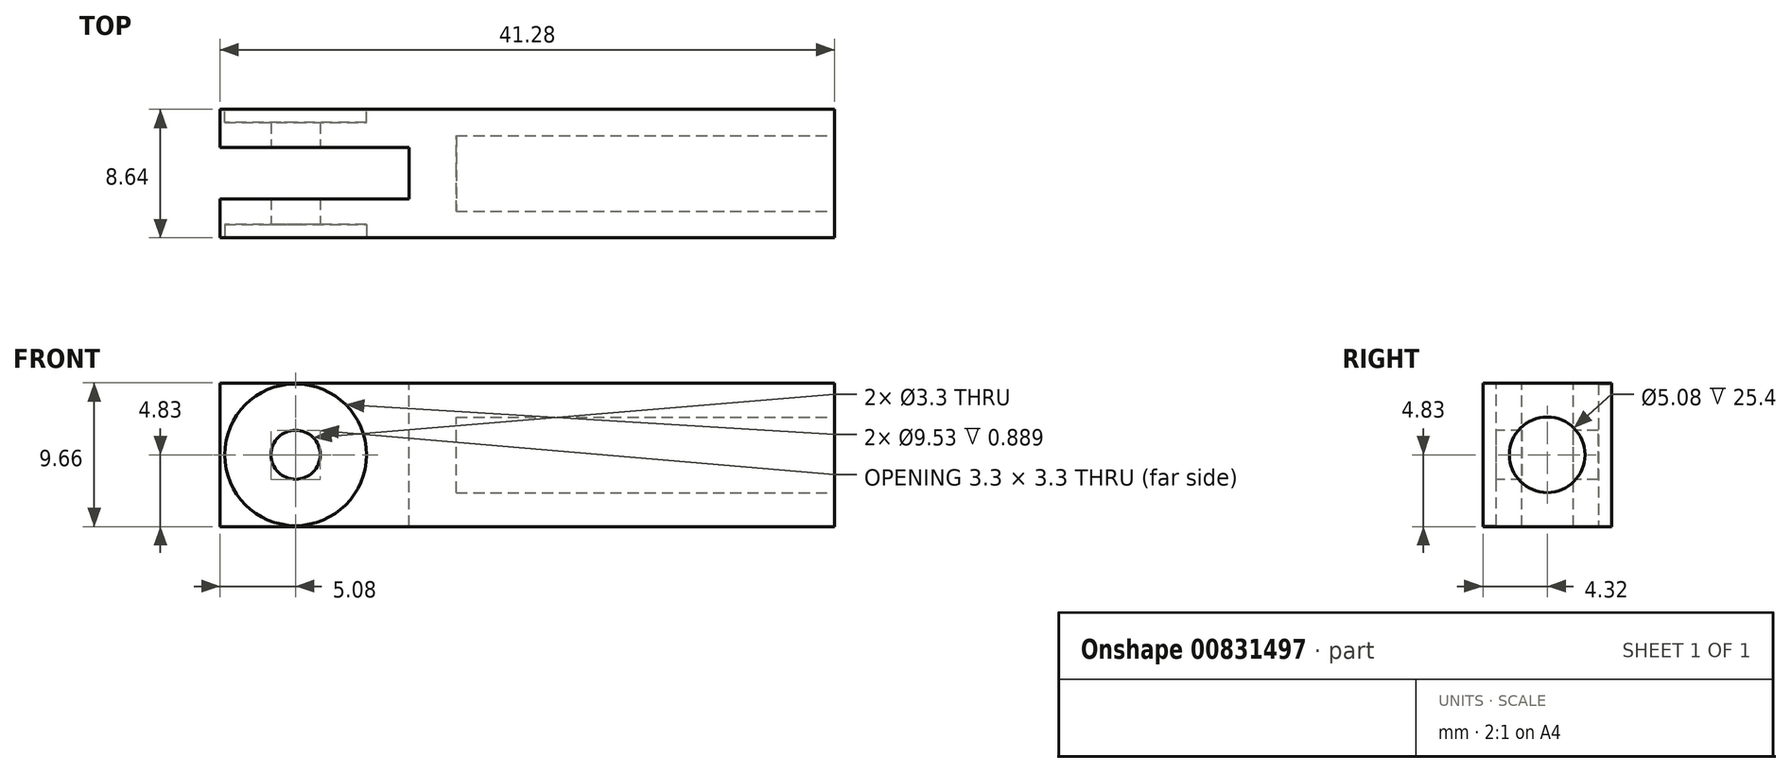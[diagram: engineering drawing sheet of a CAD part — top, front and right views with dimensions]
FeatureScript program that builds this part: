
annotation { "Feature Type Name" : "Feature", "Feature Type Description" : "" }
export const myFeature = defineFeature(function(context is Context, id is Id, definition is map)
    precondition{}
    {
        {
            var Q0;
            Q0=qCreatedBy(makeId("Right.planeOp"),FACE);
            var sketch = newSketch(context, id + "F0", { "sketchPlane" : qUnion([Q0])});
            skLineSegment(sketch, "E0.bottom", {"start": v(4.32, -4.83) * mm, "end": v(-4.32, -4.83) * mm});
            skLineSegment(sketch, "E0.top", {"start": v(4.32, 4.83) * mm, "end": v(-4.32, 4.83) * mm});
            skLineSegment(sketch, "E0.left", {"start": v(4.32, -4.83) * mm, "end": v(4.32, 4.83) * mm});
            skLineSegment(sketch, "E0.right", {"start": v(-4.32, -4.83) * mm, "end": v(-4.32, 4.83) * mm});
            skPoint(sketch, "E0.middle", {"position": v(0, 0) * mm});
            skSolve(sketch);
        }
        {
            var Q0;
            Q0 = qSketchRegion(id + "F0", true);
            extrude(context, id + "F1", {"entities" : qUnion([Q0]), "depth" : 41.27 * mm, "offsetDistance" : 25.4 * mm});
        }
        {
            var Q0;
            Q0=makeQuery(id+"F1.opExtrude","CAP_FACE",FACE,{"disambiguationData":[OSD([sQuery(id+"F0.wireOp",EDGE,"E0.bottom"),sQuery(id+"F0.wireOp",EDGE,"E0.top"),sQuery(id+"F0.wireOp",EDGE,"E0.left"),sQuery(id+"F0.wireOp",EDGE,"E0.right")])],"isStart":false});
            var sketch = newSketch(context, id + "F2", { "sketchPlane" : qUnion([Q0])});
            skCircle(sketch, "E1", {"center": v(0, 0) * mm, "radius": 2.54 * mm});
            skSolve(sketch);
        }
        {
            var Q0;
            Q0 = qSketchRegion(id + "F2", true);
            extrude(context, id + "F3", {"entities" : qUnion([Q0]), "operationType" : NewBodyOperationType.REMOVE, "oppositeDirection" : true, "depth" : 25.4 * mm, "offsetDistance" : 25.4 * mm});
        }
        {
            var Q0;
            Q0=makeQuery(id+"F1.opExtrude","SWEPT_FACE",FACE,{"disambiguationData":[OSD([sQuery(id+"F0.wireOp",EDGE,"E0.top")])]});
            var sketch = newSketch(context, id + "F4", { "sketchPlane" : qUnion([Q0])});
            skPoint(sketch, "E2.middle", {"position": v(0, 0) * mm});
            skLineSegment(sketch, "E3", {"start": v(0, 1.77) * mm, "end": v(12.71, 1.77) * mm});
            skLineSegment(sketch, "E4", {"start": v(12.71, 1.77) * mm, "end": v(12.71, -1.7) * mm});
            skLineSegment(sketch, "E5", {"start": v(12.71, -1.7) * mm, "end": v(0, -1.7) * mm});
            skSolve(sketch);
        }
        {
            var Q0;
            Q0=makeQuery(id+"F1.opExtrude","SWEPT_FACE",FACE,{"disambiguationData":[OSD([sQuery(id+"F0.wireOp",EDGE,"E0.right")])]});
            var sketch = newSketch(context, id + "F5", { "sketchPlane" : qUnion([Q0])});
            skCircle(sketch, "E6", {"center": v(5.08, 0) * mm, "radius": 1.65 * mm});
            skSolve(sketch);
        }
        {
            var Q0;
            Q0 = qSketchRegion(id + "F5", true);
            extrude(context, id + "F6", {"entities" : qUnion([Q0]), "operationType" : NewBodyOperationType.REMOVE, "oppositeDirection" : true, "depth" : 8.64 * mm, "offsetDistance" : 25.4 * mm});
        }
        {
            var Q0;
            Q0=makeQuery(id+"F1.opExtrude","SWEPT_FACE",FACE,{"disambiguationData":[OSD([sQuery(id+"F0.wireOp",EDGE,"E0.right")])]});
            var sketch = newSketch(context, id + "F7", { "sketchPlane" : qUnion([Q0])});
            skCircle(sketch, "E7", {"center": v(5.08, 0) * mm, "radius": 4.76 * mm});
            skSolve(sketch);
        }
        {
            var Q0;
            Q0 = qSketchRegion(id + "F7", true);
            extrude(context, id + "F8", {"entities" : qUnion([Q0]), "operationType" : NewBodyOperationType.REMOVE, "oppositeDirection" : true, "depth" : 0.89 * mm, "offsetDistance" : 25.4 * mm});
        }
        {
            var Q0;
            Q0=makeQuery(id+"F1.opExtrude","SWEPT_FACE",FACE,{"disambiguationData":[OSD([sQuery(id+"F0.wireOp",EDGE,"E0.left")])]});
            var sketch = newSketch(context, id + "F9", { "sketchPlane" : qUnion([Q0])});
            skCircle(sketch, "E8", {"center": v(-5.08, 0) * mm, "radius": 4.76 * mm});
            skSolve(sketch);
        }
        {
            var Q0;
            Q0 = qSketchRegion(id + "F9", true);
            extrude(context, id + "F10", {"entities" : qUnion([Q0]), "operationType" : NewBodyOperationType.REMOVE, "oppositeDirection" : true, "depth" : 0.89 * mm, "offsetDistance" : 25.4 * mm});
        }
        {
            var Q0;
            Q0 = qSketchRegion(id + "F4", true);
            var Q1;
            {var subQ0=sQuery(id+"F4.wireOp",EDGE,"E3");Q1=makeQuery(id+"F4.imprint","IMPRINT",FACE,{"disambiguationData":[TD([[makeQuery(id+"F4.imprint","IMPRINT",EDGE,{"derivedFrom":subQ0}),-1.0]])]});}
            extrude(context, id + "F11", {"entities" : qUnion([Q0, Q1]), "operationType" : NewBodyOperationType.REMOVE, "oppositeDirection" : true, "depth" : 9.65 * mm, "offsetDistance" : 25.4 * mm});
        }
    });
